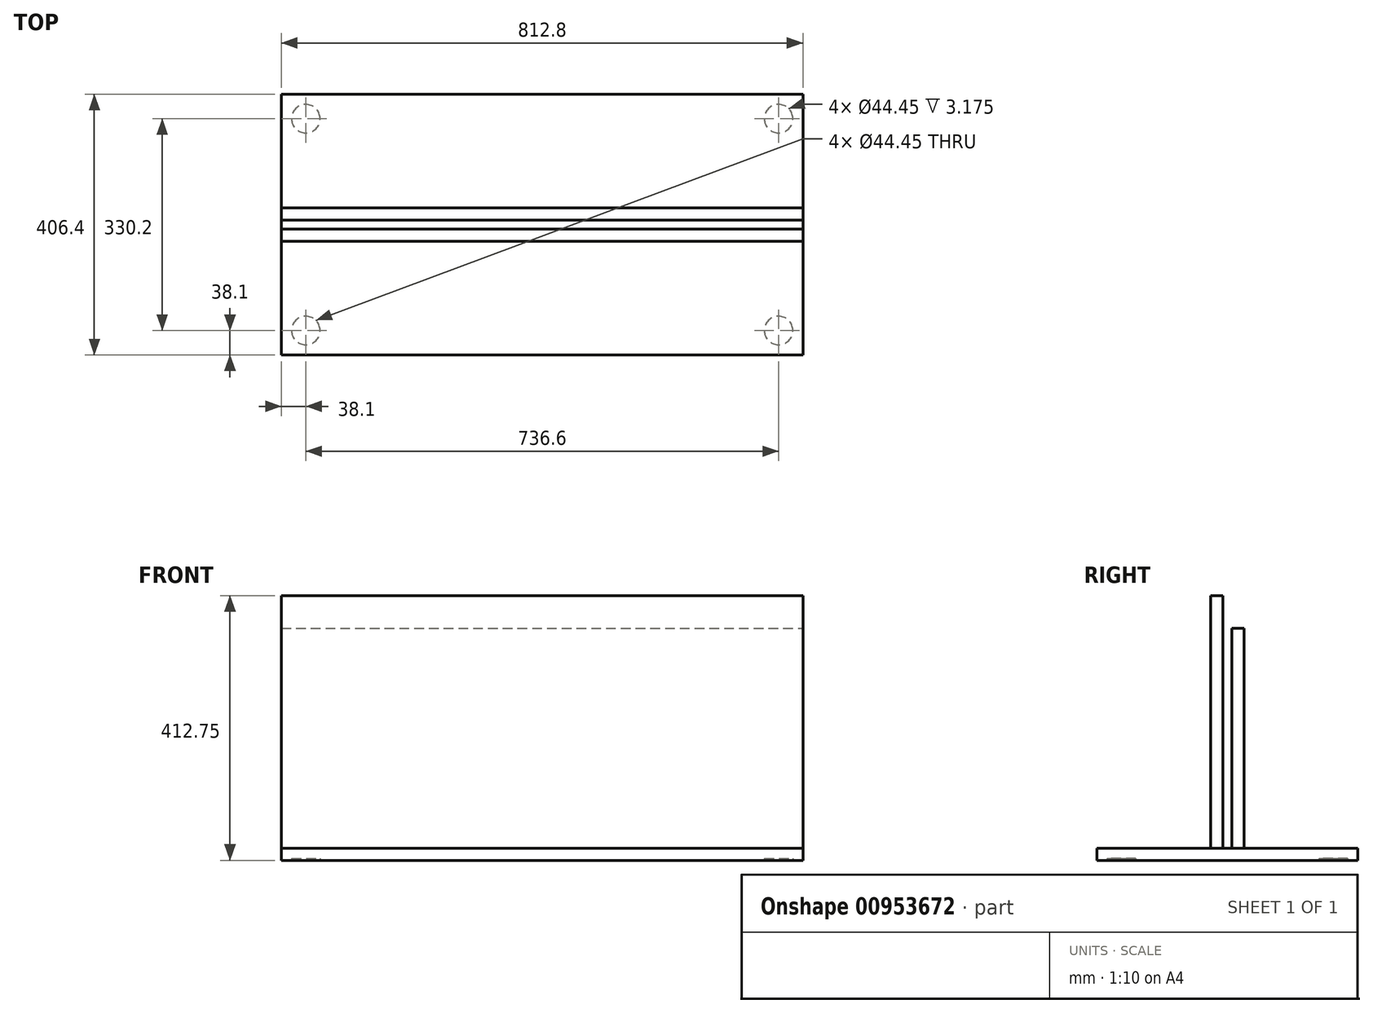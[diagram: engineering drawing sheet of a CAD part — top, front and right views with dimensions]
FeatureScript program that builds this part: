
annotation { "Feature Type Name" : "Feature", "Feature Type Description" : "" }
export const myFeature = defineFeature(function(context is Context, id is Id, definition is map)
    precondition{}
    {
        {
            var Q0;
            Q0=qCreatedBy(makeId("Top.planeOp"),FACE);
            var sketch = newSketch(context, id + "F0", { "sketchPlane" : qUnion([Q0])});
            skLineSegment(sketch, "E0.bottom", {"start": v(-406.4, -203.2) * mm, "end": v(406.4, -203.2) * mm});
            skLineSegment(sketch, "E0.top", {"start": v(-406.4, 203.2) * mm, "end": v(406.4, 203.2) * mm});
            skLineSegment(sketch, "E0.left", {"start": v(-406.4, -203.2) * mm, "end": v(-406.4, 203.2) * mm});
            skLineSegment(sketch, "E0.right", {"start": v(406.4, -203.2) * mm, "end": v(406.4, 203.2) * mm});
            skPoint(sketch, "E0.middle", {"position": v(0, 0) * mm});
            skSolve(sketch);
        }
        {
            var Q0;
            Q0=makeQuery(id+"F0.imprint","IMPRINT",FACE,{"disambiguationData":[TD([[makeQuery(id+"F0.imprint","IMPRINT",EDGE,{"derivedFrom":sQuery(id+"F0.wireOp",EDGE,"E0.bottom")}),1.0]])]});
            extrude(context, id + "F1", {"entities" : qUnion([Q0]), "depth" : 19.05 * mm, "offsetDistance" : 25.4 * mm});
        }
        {
            var Q0;
            Q0=makeQuery(id+"F1.opExtrude","CAP_FACE",FACE,{"disambiguationData":[OSD([sQuery(id+"F0.wireOp",EDGE,"E0.bottom"),sQuery(id+"F0.wireOp",EDGE,"E0.top"),sQuery(id+"F0.wireOp",EDGE,"E0.left"),sQuery(id+"F0.wireOp",EDGE,"E0.right")])],"isStart":false});
            var sketch = newSketch(context, id + "F2", { "sketchPlane" : qUnion([Q0])});
            skLineSegment(sketch, "E1.bottom", {"start": v(-406.4, 26.2) * mm, "end": v(406.4, 26.2) * mm});
            skLineSegment(sketch, "E1.top", {"start": v(-406.4, -26.2) * mm, "end": v(406.4, -26.2) * mm});
            skLineSegment(sketch, "E1.left", {"start": v(-406.4, 26.2) * mm, "end": v(-406.4, -26.2) * mm});
            skLineSegment(sketch, "E1.right", {"start": v(406.4, 26.2) * mm, "end": v(406.4, -26.2) * mm});
            skPoint(sketch, "E1.middle", {"position": v(0, 0) * mm});
            skSolve(sketch);
        }
        {
            var Q0;
            Q0 = qSketchRegion(id + "F2", true);
            extrude(context, id + "F3", {"entities" : qUnion([Q0]), "operationType" : NewBodyOperationType.REMOVE, "oppositeDirection" : true, "depth" : 0.03 * mm, "offsetDistance" : 25.4 * mm});
        }
        {
            var Q0;
            Q0=makeQuery(id+"F3.boolean.opBoolean","COPY",FACE,{"derivedFrom":makeQuery(id+"F3.opExtrude","CAP_FACE",FACE,{"disambiguationData":[OSD([sQuery(id+"F2.wireOp",EDGE,"E1.bottom"),sQuery(id+"F2.wireOp",EDGE,"E1.top"),sQuery(id+"F2.wireOp",EDGE,"E1.left"),sQuery(id+"F2.wireOp",EDGE,"E1.right")])],"isStart":false})});
            var sketch = newSketch(context, id + "F4", { "sketchPlane" : qUnion([Q0])});
            skLineSegment(sketch, "E2.bottom", {"start": v(-406.4, -26.2) * mm, "end": v(406.4, -26.2) * mm});
            skLineSegment(sketch, "E2.top", {"start": v(-406.4, -7.14) * mm, "end": v(406.4, -7.14) * mm});
            skLineSegment(sketch, "E2.left", {"start": v(-406.4, -26.2) * mm, "end": v(-406.4, -7.14) * mm});
            skLineSegment(sketch, "E2.right", {"start": v(406.4, -26.2) * mm, "end": v(406.4, -7.14) * mm});
            skLineSegment(sketch, "E3.bottom", {"start": v(-406.4, 26.2) * mm, "end": v(406.4, 26.2) * mm});
            skLineSegment(sketch, "E3.top", {"start": v(-406.4, 7.14) * mm, "end": v(406.4, 7.14) * mm});
            skLineSegment(sketch, "E3.left", {"start": v(-406.4, 26.2) * mm, "end": v(-406.4, 7.14) * mm});
            skLineSegment(sketch, "E3.right", {"start": v(406.4, 26.2) * mm, "end": v(406.4, 7.14) * mm});
            skSolve(sketch);
        }
        {
            var Q0;
            Q0 = qSketchRegion(id + "F4", true);
            extrude(context, id + "F5", {"entities" : qUnion([Q0]), "depth" : 393.7 * mm, "offsetDistance" : 25.4 * mm});
        }
        {
            var Q0;
            Q0=makeQuery(id+"F5.opExtrude","SWEPT_FACE",FACE,{"disambiguationData":[OSD([sQuery(id+"F4.wireOp",EDGE,"E3.bottom")])]});
            var sketch = newSketch(context, id + "F6", { "sketchPlane" : qUnion([Q0])});
            skLineSegment(sketch, "E4.bottom", {"start": v(406.4, 412.72) * mm, "end": v(-406.4, 412.72) * mm});
            skLineSegment(sketch, "E4.top", {"start": v(406.4, 361.92) * mm, "end": v(-406.4, 361.92) * mm});
            skLineSegment(sketch, "E4.left", {"start": v(406.4, 412.72) * mm, "end": v(406.4, 361.92) * mm});
            skLineSegment(sketch, "E4.right", {"start": v(-406.4, 412.72) * mm, "end": v(-406.4, 361.92) * mm});
            skSolve(sketch);
        }
        {
            var Q0;
            Q0 = qSketchRegion(id + "F6", true);
            var Q1;
            Q1=makeQuery(id+"F5.opExtrude","SWEPT_FACE",FACE,{"disambiguationData":[OSD([sQuery(id+"F4.wireOp",EDGE,"E3.top")])]});
            extrude(context, id + "F7", {"entities" : qUnion([Q0]), "operationType" : NewBodyOperationType.REMOVE, "endBound" : BoundingType.UP_TO_SURFACE, "oppositeDirection" : true, "depth" : 25.4 * mm, "endBoundEntityFace" : qUnion([Q1]), "offsetDistance" : 25.4 * mm});
        }
        {
            var Q0;
            Q0=makeQuery(id+"F5.opExtrude","SWEPT_FACE",FACE,{"disambiguationData":[OSD([sQuery(id+"F4.wireOp",EDGE,"E3.bottom")])]});
            var sketch = newSketch(context, id + "F8", { "sketchPlane" : qUnion([Q0])});
            skLineSegment(sketch, "E5.0.0", {"start": v(406.4, 19.02) * mm, "end": v(406.4, 361.92) * mm});
            skLineSegment(sketch, "E5.0.1", {"start": v(406.4, 361.92) * mm, "end": v(-406.4, 361.92) * mm});
            skLineSegment(sketch, "E5.0.2", {"start": v(-406.4, 361.92) * mm, "end": v(-406.4, 19.02) * mm});
            skLineSegment(sketch, "E5.0.3", {"start": v(-406.4, 19.02) * mm, "end": v(406.4, 19.02) * mm});
            skSolve(sketch);
        }
        {
            var Q0;
            Q0 = qSketchRegion(id + "F8", true);
            extrude(context, id + "F9", {"entities" : qUnion([Q0]), "depth" : 0.03 * mm, "offsetDistance" : 25.4 * mm});
        }
        {
            var Q0;
            Q0=makeQuery(id+"F5.opExtrude","SWEPT_FACE",FACE,{"disambiguationData":[OSD([sQuery(id+"F4.wireOp",EDGE,"E3.top")])]});
            var sketch = newSketch(context, id + "F10", { "sketchPlane" : qUnion([Q0])});
            skLineSegment(sketch, "E6.0.0", {"start": v(406.4, 19.02) * mm, "end": v(406.4, 361.92) * mm});
            skLineSegment(sketch, "E6.0.1", {"start": v(406.4, 361.92) * mm, "end": v(-406.4, 361.92) * mm});
            skLineSegment(sketch, "E6.0.2", {"start": v(-406.4, 361.92) * mm, "end": v(-406.4, 19.02) * mm});
            skLineSegment(sketch, "E6.0.3", {"start": v(-406.4, 19.02) * mm, "end": v(406.4, 19.02) * mm});
            skSolve(sketch);
        }
        {
            var Q0;
            Q0 = qSketchRegion(id + "F10", true);
            extrude(context, id + "F11", {"entities" : qUnion([Q0]), "depth" : 0.03 * mm, "offsetDistance" : 25.4 * mm});
        }
        {
            var Q0;
            Q0=makeQuery(id+"F5.opExtrude","SWEPT_FACE",FACE,{"disambiguationData":[OSD([sQuery(id+"F4.wireOp",EDGE,"E2.top")])]});
            var sketch = newSketch(context, id + "F12", { "sketchPlane" : qUnion([Q0])});
            skLineSegment(sketch, "E7.0.0", {"start": v(-406.4, 19.02) * mm, "end": v(406.4, 19.02) * mm});
            skLineSegment(sketch, "E7.0.1", {"start": v(406.4, 19.02) * mm, "end": v(406.4, 412.72) * mm});
            skLineSegment(sketch, "E7.0.2", {"start": v(406.4, 412.72) * mm, "end": v(-406.4, 412.72) * mm});
            skLineSegment(sketch, "E7.0.3", {"start": v(-406.4, 412.72) * mm, "end": v(-406.4, 19.02) * mm});
            skSolve(sketch);
        }
        {
            var Q0;
            Q0 = qSketchRegion(id + "F12", true);
            extrude(context, id + "F13", {"entities" : qUnion([Q0]), "depth" : 0.03 * mm, "offsetDistance" : 25.4 * mm});
        }
        {
            var Q0;
            Q0=makeQuery(id+"F5.opExtrude","SWEPT_FACE",FACE,{"disambiguationData":[OSD([sQuery(id+"F4.wireOp",EDGE,"E2.bottom")])]});
            var sketch = newSketch(context, id + "F14", { "sketchPlane" : qUnion([Q0])});
            skLineSegment(sketch, "E8.0.0", {"start": v(-406.4, 19.02) * mm, "end": v(406.4, 19.02) * mm});
            skLineSegment(sketch, "E8.0.1", {"start": v(406.4, 19.02) * mm, "end": v(406.4, 412.72) * mm});
            skLineSegment(sketch, "E8.0.2", {"start": v(406.4, 412.72) * mm, "end": v(-406.4, 412.72) * mm});
            skLineSegment(sketch, "E8.0.3", {"start": v(-406.4, 412.72) * mm, "end": v(-406.4, 19.02) * mm});
            skSolve(sketch);
        }
        {
            var Q0;
            Q0 = qSketchRegion(id + "F14", true);
            extrude(context, id + "F15", {"entities" : qUnion([Q0]), "depth" : 0.03 * mm, "offsetDistance" : 25.4 * mm});
        }
        {
            var Q0;
            {var subQ0=sQuery(id+"F0.wireOp",EDGE,"E0.bottom");var subQ1=sQuery(id+"F0.wireOp",EDGE,"E0.right");var subQ2=sQuery(id+"F0.wireOp",EDGE,"E0.left");Q0=makeQuery(id+"F3.boolean.opBoolean","SPLIT",FACE,{"disambiguationData":[TD([makeQuery(id+"F1.opExtrude","SWEPT_FACE",FACE,{"disambiguationData":[OSD([subQ0])]})])],"derivedFrom":makeQuery(id+"F1.opExtrude","CAP_FACE",FACE,{"disambiguationData":[OSD([subQ0,sQuery(id+"F0.wireOp",EDGE,"E0.top"),subQ2,subQ1])],"isStart":false})});}
            var sketch = newSketch(context, id + "F16", { "sketchPlane" : qUnion([Q0])});
            skLineSegment(sketch, "E9.bottom", {"start": v(-406.4, 203.2) * mm, "end": v(406.4, 203.2) * mm});
            skLineSegment(sketch, "E9.top", {"start": v(-406.4, -203.2) * mm, "end": v(406.4, -203.2) * mm});
            skLineSegment(sketch, "E9.left", {"start": v(-406.4, 203.2) * mm, "end": v(-406.4, -203.2) * mm});
            skLineSegment(sketch, "E9.right", {"start": v(406.4, 203.2) * mm, "end": v(406.4, -203.2) * mm});
            skPoint(sketch, "E9.middle", {"position": v(0, 0) * mm});
            skSolve(sketch);
        }
        {
            var Q0;
            Q0 = qSketchRegion(id + "F16", true);
            extrude(context, id + "F17", {"entities" : qUnion([Q0]), "depth" : 0.03 * mm, "offsetDistance" : 25.4 * mm});
        }
        {
            var Q0;
            Q0=makeQuery(id+"F1.opExtrude","CAP_FACE",FACE,{"disambiguationData":[OSD([sQuery(id+"F0.wireOp",EDGE,"E0.bottom"),sQuery(id+"F0.wireOp",EDGE,"E0.top"),sQuery(id+"F0.wireOp",EDGE,"E0.left"),sQuery(id+"F0.wireOp",EDGE,"E0.right")])],"isStart":true});
            var sketch = newSketch(context, id + "F18", { "sketchPlane" : qUnion([Q0])});
            skLineSegment(sketch, "E10.bottom", {"start": v(-368.3, 165.1) * mm, "end": v(368.3, 165.1) * mm, "construction": true});
            skLineSegment(sketch, "E10.top", {"start": v(-368.3, -165.1) * mm, "end": v(368.3, -165.1) * mm, "construction": true});
            skLineSegment(sketch, "E10.left", {"start": v(-368.3, 165.1) * mm, "end": v(-368.3, -165.1) * mm, "construction": true});
            skLineSegment(sketch, "E10.right", {"start": v(368.3, 165.1) * mm, "end": v(368.3, -165.1) * mm, "construction": true});
            skPoint(sketch, "E10.middle", {"position": v(0, 0) * mm});
            skCircle(sketch, "E11", {"center": v(-368.3, 165.1) * mm, "radius": 22.23 * mm});
            skCircle(sketch, "E12", {"center": v(-368.3, -165.1) * mm, "radius": 22.23 * mm});
            skCircle(sketch, "E13", {"center": v(368.3, -165.1) * mm, "radius": 22.23 * mm});
            skCircle(sketch, "E14", {"center": v(368.3, 165.1) * mm, "radius": 22.23 * mm});
            skSolve(sketch);
        }
        {
            var Q0;
            Q0 = qSketchRegion(id + "F18", true);
            extrude(context, id + "F19", {"entities" : qUnion([Q0]), "operationType" : NewBodyOperationType.REMOVE, "oppositeDirection" : true, "depth" : 3.17 * mm, "offsetDistance" : 25.4 * mm});
        }
        {
            var Q0;
            Q0=makeQuery(id+"F1.opExtrude","CAP_FACE",FACE,{"disambiguationData":[OSD([sQuery(id+"F0.wireOp",EDGE,"E0.bottom"),sQuery(id+"F0.wireOp",EDGE,"E0.top"),sQuery(id+"F0.wireOp",EDGE,"E0.left"),sQuery(id+"F0.wireOp",EDGE,"E0.right")])],"isStart":true});
            var sketch = newSketch(context, id + "F20", { "sketchPlane" : qUnion([Q0])});
            skLineSegment(sketch, "E15.0", {"start": v(-406.4, -203.2) * mm, "end": v(406.4, -203.2) * mm});
            skLineSegment(sketch, "E16.0", {"start": v(406.4, 203.2) * mm, "end": v(406.4, -203.2) * mm});
            skLineSegment(sketch, "E17.0", {"start": v(-406.4, 203.2) * mm, "end": v(406.4, 203.2) * mm});
            skLineSegment(sketch, "E18.0", {"start": v(-406.4, 203.2) * mm, "end": v(-406.4, -203.2) * mm});
            skCircle(sketch, "E19.0", {"center": v(-368.3, -165.1) * mm, "radius": 22.22 * mm});
            skCircle(sketch, "E20.0", {"center": v(-368.3, 165.1) * mm, "radius": 22.22 * mm});
            skCircle(sketch, "E21.0", {"center": v(368.3, -165.1) * mm, "radius": 22.22 * mm});
            skCircle(sketch, "E22.0", {"center": v(368.3, 165.1) * mm, "radius": 22.22 * mm});
            skSolve(sketch);
        }
        {
            var Q0;
            Q0 = qSketchRegion(id + "F20", true);
            extrude(context, id + "F21", {"entities" : qUnion([Q0]), "depth" : 0.03 * mm, "offsetDistance" : 25.4 * mm});
        }
    });
